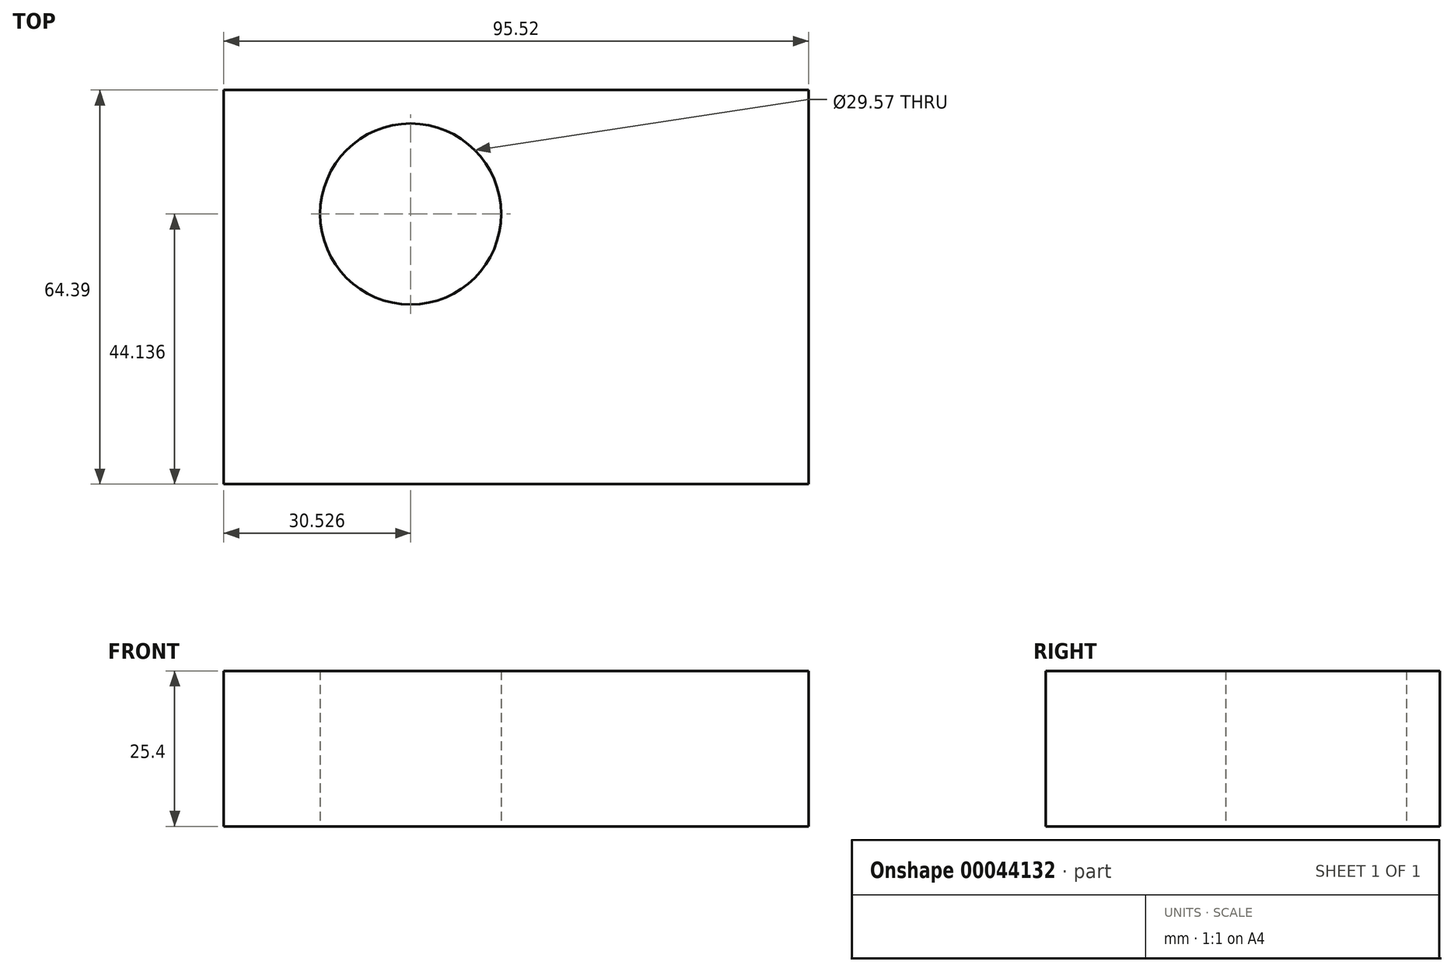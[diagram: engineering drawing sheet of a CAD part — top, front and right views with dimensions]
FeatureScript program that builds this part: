
annotation { "Feature Type Name" : "Feature", "Feature Type Description" : "" }
export const myFeature = defineFeature(function(context is Context, id is Id, definition is map)
    precondition{}
    {
        {
            var Q0;
            Q0=qCreatedBy(makeId("Top.planeOp"),FACE);
            var sketch = newSketch(context, id + "F0", { "sketchPlane" : qUnion([Q0])});
            skLineSegment(sketch, "E0.bottom", {"start": v(-41.56, 26.6) * mm, "end": v(53.96, 26.6) * mm});
            skLineSegment(sketch, "E0.top", {"start": v(-41.56, -37.79) * mm, "end": v(53.96, -37.79) * mm});
            skLineSegment(sketch, "E0.left", {"start": v(-41.56, 26.6) * mm, "end": v(-41.56, -37.79) * mm});
            skLineSegment(sketch, "E0.right", {"start": v(53.96, 26.6) * mm, "end": v(53.96, -37.79) * mm});
            skCircle(sketch, "E1", {"center": v(-11.03, 6.35) * mm, "radius": 14.79 * mm});
            skSolve(sketch);
        }
        {
            var Q0;
            Q0=makeQuery(id+"F0.imprint","IMPRINT",FACE,{"disambiguationData":[TD([[makeQuery(id+"F0.imprint","IMPRINT",EDGE,{"derivedFrom":sQuery(id+"F0.wireOp",EDGE,"E0.bottom")}),-1.0]])]});
            extrude(context, id + "F1", {"entities" : qUnion([Q0]), "depth" : 25.4 * mm});
        }
    });
